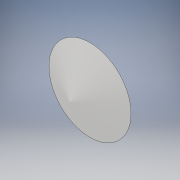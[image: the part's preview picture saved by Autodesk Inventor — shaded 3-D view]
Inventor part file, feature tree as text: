
AUTODESK INVENTOR PART (.ipt)
format: ipt  version: 2018 (Build 220112000, 112)  size: 100,352 bytes
history: native  units: mm
features: revolve x1, sketch x1
ambient origin geometry x8: Origin, YZ Plane, XZ Plane, XY Plane, X Axis, Y Axis, Z Axis, Center Point
bodies: Volumenkörper1 (feature_tree)
feature tree (2):
  revolve  "Umdrehung1"
  sketch  "Skizze1"  dims[d4=40.0mm d5=40.0mm d7=360.0deg]
